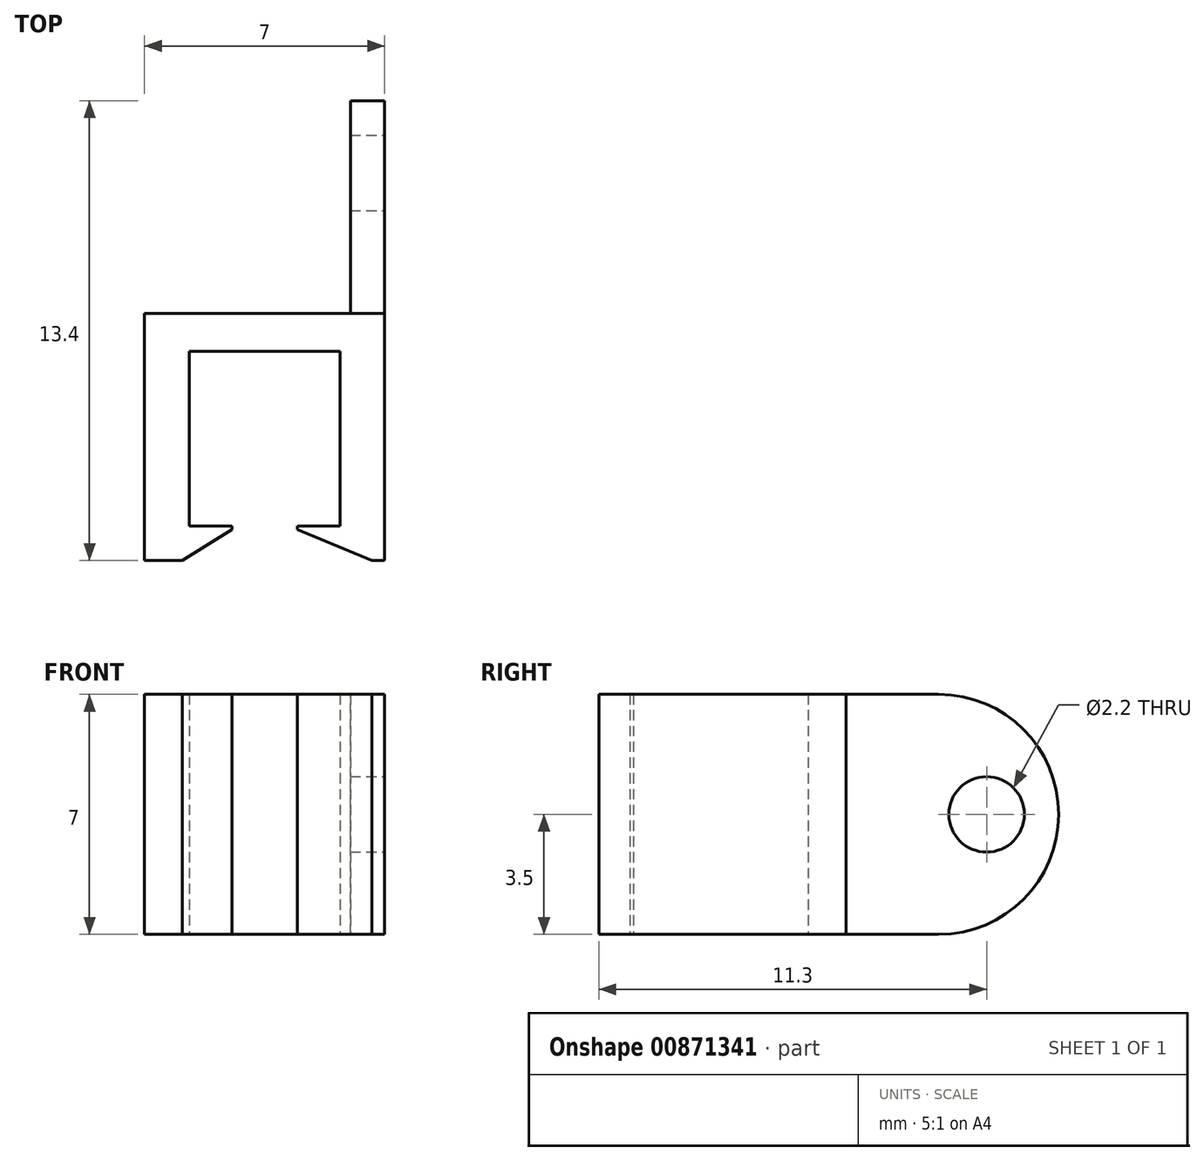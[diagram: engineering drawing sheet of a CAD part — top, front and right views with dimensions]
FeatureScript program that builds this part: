
annotation { "Feature Type Name" : "Feature", "Feature Type Description" : "" }
export const myFeature = defineFeature(function(context is Context, id is Id, definition is map)
    precondition{}
    {
        {
            var Q0;
            Q0=qCreatedBy(makeId("Top.planeOp"),FACE);
            var sketch = newSketch(context, id + "F0", { "sketchPlane" : qUnion([Q0])});
            skLineSegment(sketch, "E0", {"start": v(-2.2, -6.2) * mm, "end": v(-0.95, -6.2) * mm});
            skLineSegment(sketch, "E1", {"start": v(-0.95, -6.2) * mm, "end": v(-0.95, -6.3) * mm});
            skLineSegment(sketch, "E2", {"start": v(-2.4, -7.2) * mm, "end": v(-0.95, -6.3) * mm});
            skLineSegment(sketch, "E3", {"start": v(-2.4, -7.2) * mm, "end": v(-3.5, -7.2) * mm});
            skLineSegment(sketch, "E4", {"start": v(-3.5, -7.2) * mm, "end": v(-3.5, 0) * mm});
            skLineSegment(sketch, "E5", {"start": v(-3.5, 0) * mm, "end": v(3.5, 0) * mm});
            skLineSegment(sketch, "E6", {"start": v(3.5, 0) * mm, "end": v(3.5, -7.2) * mm});
            skLineSegment(sketch, "E7", {"start": v(3.5, -7.2) * mm, "end": v(3.12, -7.2) * mm});
            skLineSegment(sketch, "E8", {"start": v(0.95, -6.3) * mm, "end": v(3.12, -7.2) * mm});
            skLineSegment(sketch, "E9", {"start": v(0.95, -6.3) * mm, "end": v(0.95, -6.2) * mm});
            skLineSegment(sketch, "E10", {"start": v(0.95, -6.2) * mm, "end": v(2.2, -6.2) * mm});
            skLineSegment(sketch, "E11", {"start": v(2.2, -6.2) * mm, "end": v(2.2, -1.1) * mm});
            skLineSegment(sketch, "E12", {"start": v(2.2, -1.1) * mm, "end": v(-2.2, -1.1) * mm});
            skLineSegment(sketch, "E13", {"start": v(-2.2, -1.1) * mm, "end": v(-2.2, -6.2) * mm});
            skSolve(sketch);
        }
        {
            var Q0;
            Q0=makeQuery(id+"F0.imprint","IMPRINT",FACE,{"disambiguationData":[TD([[makeQuery(id+"F0.imprint","IMPRINT",EDGE,{"derivedFrom":sQuery(id+"F0.wireOp",EDGE,"E0")}),-1.0]])]});
            extrude(context, id + "F1", {"entities" : qUnion([Q0]), "endBound" : BoundingType.SYMMETRIC, "depth" : 7 * mm, "offsetDistance" : 25 * mm});
        }
        {
            var Q0;
            Q0=makeQuery(id+"F1.opExtrude","SWEPT_FACE",FACE,{"disambiguationData":[OSD([sQuery(id+"F0.wireOp",EDGE,"E6")])]});
            var sketch = newSketch(context, id + "F2", { "sketchPlane" : qUnion([Q0])});
            skLineSegment(sketch, "E14", {"start": v(0, 3.5) * mm, "end": v(2.7, 3.5) * mm});
            skLineSegment(sketch, "E15", {"start": v(0, -3.5) * mm, "end": v(2.7, -3.5) * mm});
            skArc(sketch, "E16", {"start": v(2.7, -3.5) * mm, "mid": v(6.2, 0) * mm, "end": v(2.7, 3.5) * mm});
            skCircle(sketch, "E17", {"center": v(4.1, 0) * mm, "radius": 1.1 * mm});
            skSolve(sketch);
        }
        {
            var Q0;
            Q0=makeQuery(id+"F2.imprint","IMPRINT",FACE,{"disambiguationData":[TD([[makeQuery(id+"F2.imprint","IMPRINT",EDGE,{"derivedFrom":sQuery(id+"F2.wireOp",EDGE,"E14")}),-1.0]])]});
            extrude(context, id + "F3", {"entities" : qUnion([Q0]), "oppositeDirection" : true, "depth" : 1 * mm, "offsetDistance" : 25 * mm});
        }
    });
